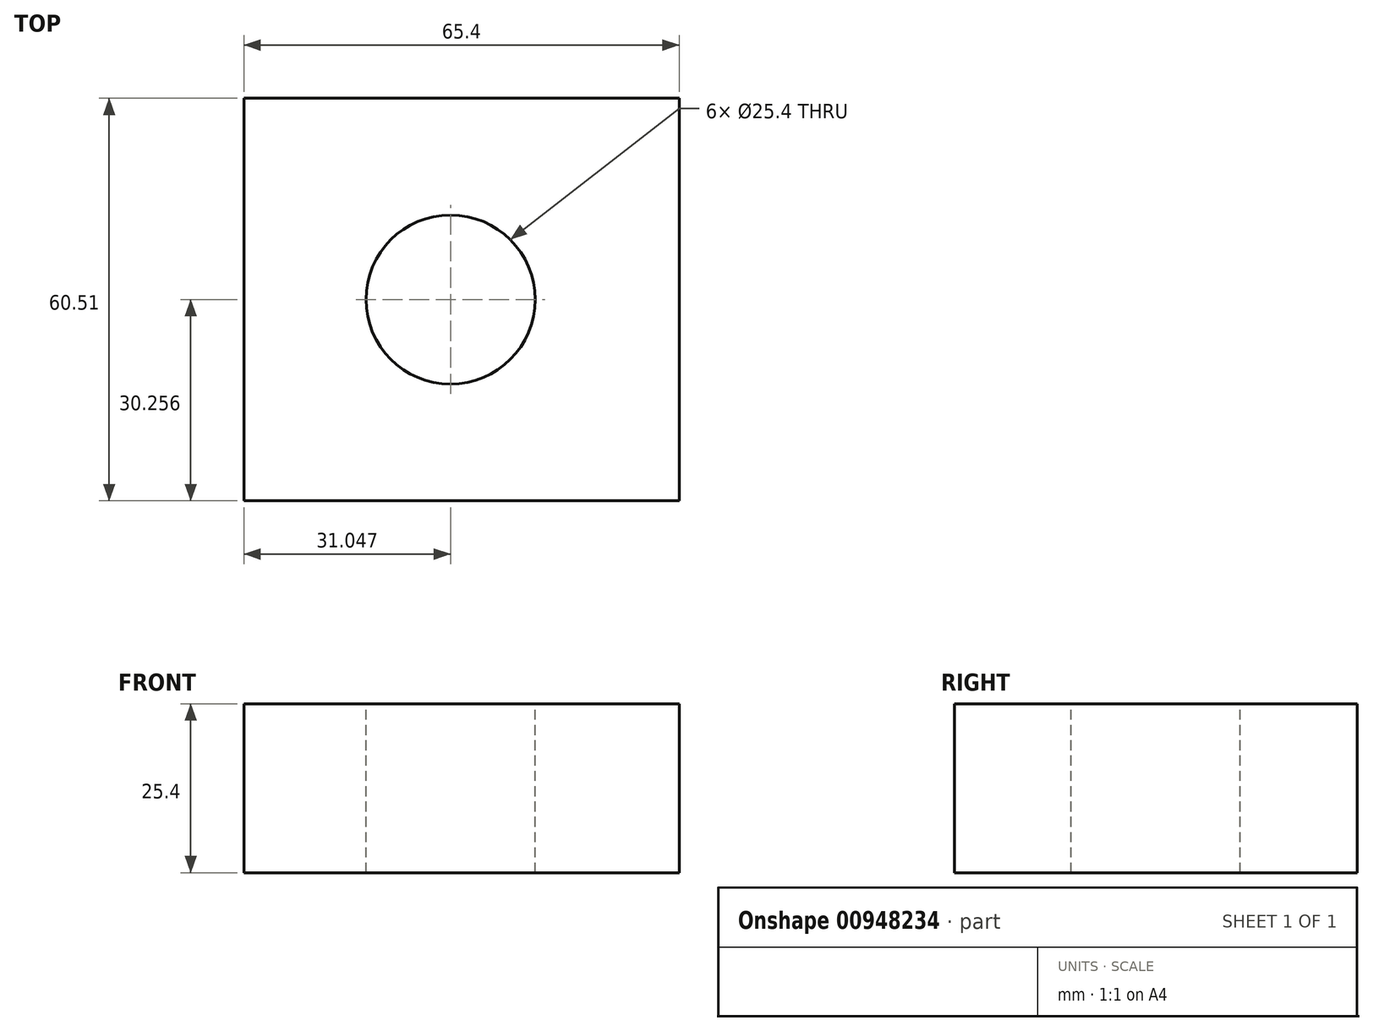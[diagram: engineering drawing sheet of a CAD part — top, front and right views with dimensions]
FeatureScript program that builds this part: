
annotation { "Feature Type Name" : "Feature", "Feature Type Description" : "" }
export const myFeature = defineFeature(function(context is Context, id is Id, definition is map)
    precondition{}
    {
        {
            var Q0;
            Q0=qCreatedBy(makeId("Top.planeOp"),FACE);
            var sketch = newSketch(context, id + "F0", { "sketchPlane" : qUnion([Q0])});
            skLineSegment(sketch, "E0.bottom", {"start": v(0, 0) * mm, "end": v(65.4, 0) * mm});
            skLineSegment(sketch, "E0.top", {"start": v(0, 60.51) * mm, "end": v(65.4, 60.51) * mm});
            skLineSegment(sketch, "E0.left", {"start": v(0, 0) * mm, "end": v(0, 60.51) * mm});
            skLineSegment(sketch, "E0.right", {"start": v(65.4, 0) * mm, "end": v(65.4, 60.51) * mm});
            skSolve(sketch);
        }
        {
            var Q0;
            Q0=makeQuery(id+"F0.imprint","IMPRINT",FACE,{"disambiguationData":[TD([[makeQuery(id+"F0.imprint","IMPRINT",EDGE,{"derivedFrom":sQuery(id+"F0.wireOp",EDGE,"E0.bottom")}),1.0]])]});
            extrude(context, id + "F1", {"entities" : qUnion([Q0]), "depth" : 25.4 * mm, "offsetDistance" : 25.4 * mm});
        }
        {
            var Q0;
            Q0=makeQuery(id+"F1.opExtrude","CAP_FACE",FACE,{"disambiguationData":[OSD([sQuery(id+"F0.wireOp",EDGE,"E0.bottom"),sQuery(id+"F0.wireOp",EDGE,"E0.top"),sQuery(id+"F0.wireOp",EDGE,"E0.left"),sQuery(id+"F0.wireOp",EDGE,"E0.right")])],"isStart":false});
            var sketch = newSketch(context, id + "F2", { "sketchPlane" : qUnion([Q0])});
            skCircle(sketch, "E1", {"center": v(31.05, 30.26) * mm, "radius": 12.7 * mm});
            skPoint(sketch, "E1.centerSnap0", {"position": v(65.4, 30.26) * mm});
            skSolve(sketch);
        }
        {
            var Q0;
            Q0 = qSketchRegion(id + "F2", true);
            extrude(context, id + "F3", {"entities" : qUnion([Q0]), "operationType" : NewBodyOperationType.REMOVE, "oppositeDirection" : true, "depth" : 25.4 * mm, "offsetDistance" : 25.4 * mm});
        }
    });
